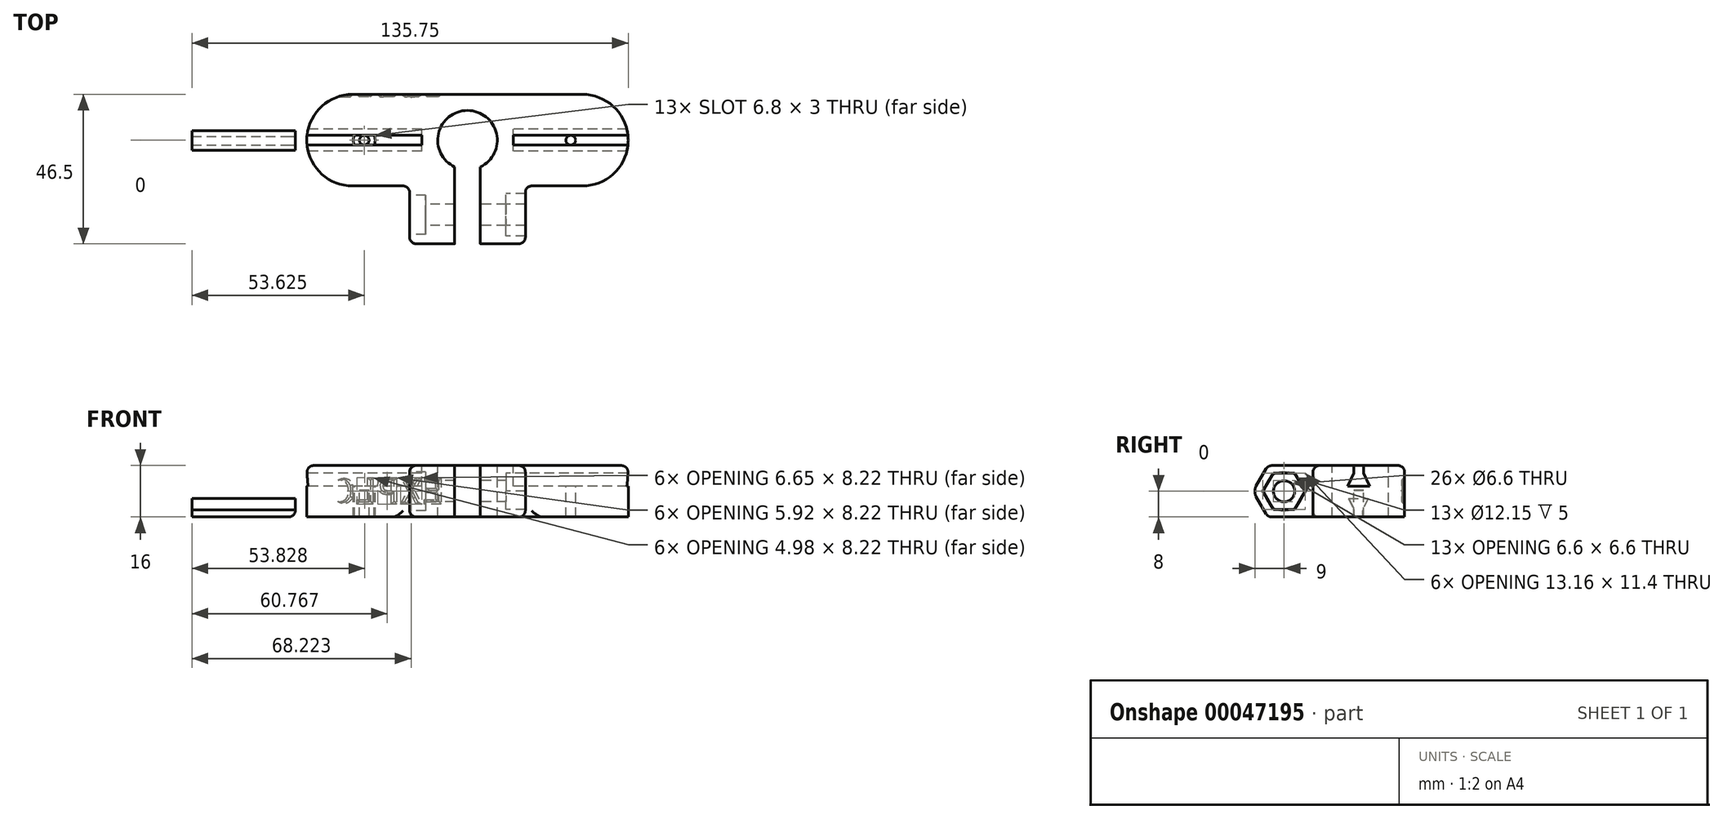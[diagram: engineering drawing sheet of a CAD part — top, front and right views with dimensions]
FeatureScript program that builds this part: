
annotation { "Feature Type Name" : "Feature", "Feature Type Description" : "" }
export const myFeature = defineFeature(function(context is Context, id is Id, definition is map)
    precondition{}
    {
        {
            assignVariable(context, id + "F0", {"name" : "PrintingOffset", "anyValue" : .4});
        }
        {
            assignVariable(context, id + "F1", {"name" : "BoltExtensionWidth", "anyValue" : 14});
        }
        {
            assignVariable(context, id + "F2", {"name" : "DeviceWidth", "anyValue" : 100});
        }
        {
            assignVariable(context, id + "F3", {"name" : "FlexureOpening", "anyValue" : 8});
        }
        {
            assignVariable(context, id + "F4", {"name" : "RodPadding", "anyValue" : 5});
        }
        {
            assignVariable(context, id + "F5", {"name" : "RodDiameter", "anyValue" : 18.5});
        }
        {
            var Q0;
            Q0=qCreatedBy(makeId("Top.planeOp"),FACE);
            var sketch = newSketch(context, id + "F6", { "sketchPlane" : qUnion([Q0])});
            skLineSegment(sketch, "E0", {"start": v(-50, 14.25) * mm, "end": v(-50, -14.25) * mm});
            skLineSegment(sketch, "E1", {"start": v(-50, -14.25) * mm, "end": v(-18, -14.25) * mm});
            skLineSegment(sketch, "E2", {"start": v(-18, -14.25) * mm, "end": v(-18, -32.25) * mm});
            skLineSegment(sketch, "E3", {"start": v(-18, -32.25) * mm, "end": v(-4, -32.25) * mm});
            skLineSegment(sketch, "E4", {"start": v(-4, -32.25) * mm, "end": v(-4, -8.34) * mm});
            skLineSegment(sketch, "E5", {"start": v(-50, 14.25) * mm, "end": v(0, 14.25) * mm});
            skLineSegment(sketch, "E6", {"start": v(0, 35.83) * mm, "end": v(0, -44.2) * mm, "construction": true});
            skLineSegment(sketch, "E7.MirrorCS", {"start": v(50, 14.25) * mm, "end": v(50, -14.25) * mm});
            skLineSegment(sketch, "E8.MirrorCS", {"start": v(50, -14.25) * mm, "end": v(18, -14.25) * mm});
            skLineSegment(sketch, "E9.MirrorCS", {"start": v(18, -14.25) * mm, "end": v(18, -32.25) * mm});
            skLineSegment(sketch, "E10.MirrorCS", {"start": v(18, -32.25) * mm, "end": v(4, -32.25) * mm});
            skLineSegment(sketch, "E11.MirrorCS", {"start": v(4, -32.25) * mm, "end": v(4, -8.34) * mm});
            skLineSegment(sketch, "E12.MirrorCS", {"start": v(50, 14.25) * mm, "end": v(0, 14.25) * mm});
            skArc(sketch, "E13", {"start": v(4, -8.34) * mm, "mid": v(0, 9.25) * mm, "end": v(-4, -8.34) * mm});
            skPoint(sketch, "E14.end.orphan", {"position": v(0, -14.88) * mm});
            skSolve(sketch);
        }
        {
            assignVariable(context, id + "F7", {"name" : "DeviceThickness", "anyValue" : 16});
        }
        {
            var Q0;
            Q0=makeQuery(id+"F6.imprint","IMPRINT",FACE,{"disambiguationData":[TD([[makeQuery(id+"F6.imprint","IMPRINT",EDGE,{"derivedFrom":sQuery(id+"F6.wireOp",EDGE,"E0")}),1.0]])]});
            extrude(context, id + "F8", {"entities" : qUnion([Q0]), "depth" : (getVariable(context, 'DeviceThickness')) * mm});
        }
        {
            assignVariable(context, id + "F9", {"name" : "NailHeadThickness", "anyValue" : 1.25});
        }
        {
            assignVariable(context, id + "F10", {"name" : "NailInsertDepth", "anyValue" : getVariable(context, 'DeviceThickness') * (2 / 5)});
        }
        {
            var Q0;
            Q0=makeQuery(id+"F8.opExtrude","SWEPT_FACE",FACE,{"disambiguationData":[OSD([sQuery(id+"F6.wireOp",EDGE,"E7.MirrorCS")])]});
            var sketch = newSketch(context, id + "F11", { "sketchPlane" : qUnion([Q0])});
            skLineSegment(sketch, "E15.1", {"start": v(14.25, 0) * mm, "end": v(-14.25, 0) * mm});
            skLineSegment(sketch, "E15.5", {"start": v(14.25, 16) * mm, "end": v(-14.25, 16) * mm});
            skLineSegment(sketch, "E15.6", {"start": v(14.25, 16) * mm, "end": v(14.25, 0) * mm});
            skLineSegment(sketch, "E15.7", {"start": v(-14.25, 16) * mm, "end": v(-14.25, 0) * mm});
            skLineSegment(sketch, "E16", {"start": v(0, 0) * mm, "end": v(0, 16) * mm, "construction": true});
            skLineSegment(sketch, "E17", {"start": v(0, 6.4) * mm, "end": v(3.4, 6.4) * mm});
            skLineSegment(sketch, "E18", {"start": v(3.4, 6.4) * mm, "end": v(1.5, 2.4) * mm});
            skLineSegment(sketch, "E19", {"start": v(1.5, 2.4) * mm, "end": v(1.5, 0) * mm});
            skLineSegment(sketch, "E20.MirrorCS", {"start": v(0, 6.4) * mm, "end": v(-3.4, 6.4) * mm});
            skLineSegment(sketch, "E21.MirrorCS", {"start": v(-1.5, 2.4) * mm, "end": v(-1.5, 0) * mm});
            skLineSegment(sketch, "E22.MirrorCS", {"start": v(-3.4, 6.4) * mm, "end": v(-1.5, 2.4) * mm});
            skLineSegment(sketch, "E23", {"start": v(-14.25, 8) * mm, "end": v(14.25, 8) * mm, "construction": true});
            skSolve(sketch);
        }
        {
            assignVariable(context, id + "F12", {"name" : "BoltShaftDiameter", "anyValue" : 6.2 + getVariable(context, 'PrintingOffset')});
        }
        {
            assignVariable(context, id + "F13", {"name" : "BoltHeadDiameter", "anyValue" : 11.75 + getVariable(context, 'PrintingOffset')});
        }
        {
            assignVariable(context, id + "F14", {"name" : "BoltHeadDepth", "anyValue" : 4.6 + getVariable(context, 'PrintingOffset')});
        }
        {
            assignVariable(context, id + "F15", {"name" : "HexNutDepth", "anyValue" : 5.6 + getVariable(context, 'PrintingOffset')});
        }
        {
            var Q0;
            Q0=makeQuery(id+"F8.opExtrude","SWEPT_FACE",FACE,{"disambiguationData":[OSD([sQuery(id+"F6.wireOp",EDGE,"E9.MirrorCS")])]});
            var sketch = newSketch(context, id + "F16", { "sketchPlane" : qUnion([Q0])});
            skLineSegment(sketch, "E24.0", {"start": v(-32.25, 16) * mm, "end": v(-32.25, 0) * mm, "construction": true});
            skLineSegment(sketch, "E24.1", {"start": v(-14.25, 0) * mm, "end": v(-32.25, 0) * mm, "construction": true});
            skLineSegment(sketch, "E24.2", {"start": v(-14.25, 16) * mm, "end": v(-14.25, 0) * mm, "construction": true});
            skLineSegment(sketch, "E24.3", {"start": v(-14.25, 16) * mm, "end": v(-32.25, 16) * mm, "construction": true});
            skLineSegment(sketch, "E25", {"start": v(-32.25, 8) * mm, "end": v(-14.25, 8) * mm, "construction": true});
            skLineSegment(sketch, "E26", {"start": v(-23.25, 16) * mm, "end": v(-23.25, 0) * mm, "construction": true});
            skPoint(sketch, "E27", {"position": v(-23.25, 8) * mm});
            skCircle(sketch, "E28.cCircle", {"center": v(-23.25, 8) * mm, "radius": 5.7 * mm, "construction": true});
            skLineSegment(sketch, "E28.0", {"start": v(-19.96, 13.7) * mm, "end": v(-16.67, 8) * mm});
            skLineSegment(sketch, "E28.1", {"start": v(-16.67, 8) * mm, "end": v(-19.96, 2.3) * mm});
            skLineSegment(sketch, "E28.2", {"start": v(-19.96, 2.3) * mm, "end": v(-26.54, 2.3) * mm});
            skLineSegment(sketch, "E28.3", {"start": v(-26.54, 2.3) * mm, "end": v(-29.83, 8) * mm});
            skLineSegment(sketch, "E28.4", {"start": v(-29.83, 8) * mm, "end": v(-26.54, 13.7) * mm});
            skLineSegment(sketch, "E28.5", {"start": v(-26.54, 13.7) * mm, "end": v(-19.96, 13.7) * mm});
            skPoint(sketch, "E28.0.midPoint", {"position": v(-18.31, 10.85) * mm});
            skSolve(sketch);
        }
        {
            var Q0;
            Q0=makeQuery(id+"F16.imprint","IMPRINT",FACE,{"disambiguationData":[TD([[makeQuery(id+"F16.imprint","IMPRINT",EDGE,{"derivedFrom":sQuery(id+"F16.wireOp",EDGE,"E28.0")}),-1.0]])]});
            extrude(context, id + "F17", {"entities" : qUnion([Q0]), "operationType" : NewBodyOperationType.REMOVE, "oppositeDirection" : true, "depth" : ((getVariable(context, 'BoltExtensionWidth') * 2) + getVariable(context, 'FlexureOpening')) * mm, "hasSecondDirection" : true, "secondDirectionOppositeDirection" : true, "secondDirectionDepth" : (((getVariable(context, 'BoltExtensionWidth') * 2) + getVariable(context, 'FlexureOpening')) - getVariable(context, 'HexNutDepth')) * mm});
        }
        {
            var Q0;
            Q0=sQuery(id+"F16.wireOp",VERTEX,"E27");
            var Q1;
            Q1=makeQuery(id+"F8.opExtrude","SWEPT_BODY",BODY,{"disambiguationData":[OSD([sQuery(id+"F6.wireOp",EDGE,"E0"),sQuery(id+"F6.wireOp",EDGE,"E1"),sQuery(id+"F6.wireOp",EDGE,"E2"),sQuery(id+"F6.wireOp",EDGE,"E3"),sQuery(id+"F6.wireOp",EDGE,"E4"),sQuery(id+"F6.wireOp",EDGE,"E5"),sQuery(id+"F6.wireOp",EDGE,"E7.MirrorCS"),sQuery(id+"F6.wireOp",EDGE,"E8.MirrorCS"),sQuery(id+"F6.wireOp",EDGE,"E9.MirrorCS"),sQuery(id+"F6.wireOp",EDGE,"E10.MirrorCS"),sQuery(id+"F6.wireOp",EDGE,"E11.MirrorCS"),sQuery(id+"F6.wireOp",EDGE,"E12.MirrorCS"),sQuery(id+"F6.wireOp",EDGE,"E13")])]});
            hole(context, id + "F18", {"style" : HoleStyle.C_BORE, "holeDiameter" : (getVariable(context, 'BoltShaftDiameter')) * mm, "cBoreDiameter" : (getVariable(context, 'BoltHeadDiameter')) * mm, "cBoreDepth" : (getVariable(context, 'BoltHeadDepth')) * mm, "endStyle" : HoleEndStyle.THROUGH, "locations" : qUnion([Q0]), "scope" : qUnion([Q1])});
        }
        {
            assignVariable(context, id + "F19", {"name" : "NailInsertWidth", "anyValue" : ((getVariable(context, 'DeviceWidth') - getVariable(context, 'RodDiameter')) - (getVariable(context, 'RodPadding') * 2)) / 2});
        }
        {
            var Q0;
            Q0=makeQuery(id+"F11.imprint","IMPRINT",FACE,{"disambiguationData":[TD([[makeQuery(id+"F11.imprint","IMPRINT",EDGE,{"derivedFrom":sQuery(id+"F11.wireOp",EDGE,"E17")}),-1.0]])]});
            extrude(context, id + "F20", {"entities" : qUnion([Q0]), "operationType" : NewBodyOperationType.REMOVE, "oppositeDirection" : true, "depth" : (getVariable(context, 'NailInsertWidth')) * mm});
        }
        {
            var Q0;
            Q0=makeQuery(id+"F11.imprint","IMPRINT",FACE,{"disambiguationData":[TD([[makeQuery(id+"F11.imprint","IMPRINT",EDGE,{"derivedFrom":sQuery(id+"F11.wireOp",EDGE,"E17")}),-1.0]])]});
            var Q1;
            Q1=makeQuery(id+"F8.opExtrude","SWEPT_FACE",FACE,{"disambiguationData":[OSD([sQuery(id+"F6.wireOp",EDGE,"E0")])]});
            extrude(context, id + "F21", {"entities" : qUnion([Q0]), "operationType" : NewBodyOperationType.REMOVE, "endBound" : BoundingType.UP_TO_SURFACE, "oppositeDirection" : true, "endBoundEntityFace" : qUnion([Q1]), "depth" : 25 * mm, "hasSecondDirection" : true, "secondDirectionOppositeDirection" : true, "secondDirectionDepth" : (getVariable(context, 'DeviceWidth') - getVariable(context, 'NailInsertWidth')) * mm});
        }
        {
            var Q0;
            Q0=makeQuery(id+"F8.opExtrude","CAP_FACE",FACE,{"disambiguationData":[OSD([sQuery(id+"F6.wireOp",EDGE,"E0"),sQuery(id+"F6.wireOp",EDGE,"E1"),sQuery(id+"F6.wireOp",EDGE,"E2"),sQuery(id+"F6.wireOp",EDGE,"E3"),sQuery(id+"F6.wireOp",EDGE,"E4"),sQuery(id+"F6.wireOp",EDGE,"E5"),sQuery(id+"F6.wireOp",EDGE,"E7.MirrorCS"),sQuery(id+"F6.wireOp",EDGE,"E8.MirrorCS"),sQuery(id+"F6.wireOp",EDGE,"E9.MirrorCS"),sQuery(id+"F6.wireOp",EDGE,"E10.MirrorCS"),sQuery(id+"F6.wireOp",EDGE,"E11.MirrorCS"),sQuery(id+"F6.wireOp",EDGE,"E12.MirrorCS"),sQuery(id+"F6.wireOp",EDGE,"E13")])],"isStart":true});
            var sketch = newSketch(context, id + "F22", { "sketchPlane" : qUnion([Q0])});
            skLineSegment(sketch, "E29", {"start": v(0, 39.53) * mm, "end": v(0, -28.34) * mm, "construction": true});
            skCircle(sketch, "E30", {"center": v(-32.12, 0) * mm, "radius": 3.4 * mm});
            skLineSegment(sketch, "E31.0", {"start": v(-50, -1.5) * mm, "end": v(-14.25, -1.5) * mm, "construction": true});
            skLineSegment(sketch, "E31.1", {"start": v(-14.25, -1.5) * mm, "end": v(-14.25, 1.5) * mm, "construction": true});
            skLineSegment(sketch, "E31.2", {"start": v(-50, 1.5) * mm, "end": v(-14.25, 1.5) * mm, "construction": true});
            skCircle(sketch, "E32", {"center": v(-32.12, 0) * mm, "radius": 1.5 * mm});
            skCircle(sketch, "E33.MirrorC", {"center": v(32.13, 0) * mm, "radius": 1.5 * mm});
            skCircle(sketch, "E34.MirrorC", {"center": v(32.13, 0) * mm, "radius": 3.4 * mm});
            skSolve(sketch);
        }
        {
            var Q0;
            {var subQ0=sQuery(id+"F11.wireOp",EDGE,"E15.1");var subQ1=makeQuery(id+"F21.boolean.opBoolean","COPY",EDGE,{"derivedFrom":makeQuery(id+"F21.opExtrude","SWEPT_EDGE",EDGE,{"disambiguationData":[OSD([subQ0,sQuery(id+"F11.wireOp",EDGE,"E21.MirrorCS")])]})});var subQ4=sQuery(id+"F22.wireOp",EDGE,"E30");var subQ5=makeQuery(id+"F22.imprint","INTERSECT",VERTEX,{"disambiguationData":[OD(0.0)],"derivedFrom":[subQ1,subQ4]});Q0=makeQuery(id+"F22.imprint","IMPRINT",FACE,{"disambiguationData":[TD([[makeQuery(id+"F22.imprint","IMPRINT",EDGE,{"disambiguationData":[TD([[subQ5,-1.0]])],"derivedFrom":subQ4}),1.0]])]});}
            var Q1;
            {var subQ0=makeQuery(id+"F21.boolean.opBoolean","COPY",EDGE,{"derivedFrom":makeQuery(id+"F21.opExtrude","SWEPT_EDGE",EDGE,{"disambiguationData":[OSD([sQuery(id+"F11.wireOp",EDGE,"E15.1"),sQuery(id+"F11.wireOp",EDGE,"E19")])]})});var subQ2=sQuery(id+"F22.wireOp",EDGE,"E30");var subQ3=makeQuery(id+"F22.imprint","INTERSECT",VERTEX,{"disambiguationData":[OD(0.0)],"derivedFrom":[subQ0,subQ2]});Q1=makeQuery(id+"F22.imprint","IMPRINT",FACE,{"disambiguationData":[TD([[makeQuery(id+"F22.imprint","IMPRINT",EDGE,{"disambiguationData":[TD([[subQ3,-1.0]])],"derivedFrom":subQ2}),1.0]])]});}
            var Q2;
            {var subQ0=sQuery(id+"F11.wireOp",EDGE,"E15.1");var subQ1=makeQuery(id+"F21.boolean.opBoolean","COPY",EDGE,{"derivedFrom":makeQuery(id+"F21.opExtrude","SWEPT_EDGE",EDGE,{"disambiguationData":[OSD([subQ0,sQuery(id+"F11.wireOp",EDGE,"E21.MirrorCS")])]})});var subQ4=sQuery(id+"F22.wireOp",EDGE,"E30");var subQ5=makeQuery(id+"F22.imprint","INTERSECT",VERTEX,{"disambiguationData":[OD(1.0)],"derivedFrom":[subQ1,subQ4]});Q2=makeQuery(id+"F22.imprint","IMPRINT",FACE,{"disambiguationData":[TD([[makeQuery(id+"F22.imprint","IMPRINT",EDGE,{"disambiguationData":[TD([[subQ5,1.0]])],"derivedFrom":subQ4}),1.0]])]});}
            var Q3;
            {var subQ0=makeQuery(id+"F21.boolean.opBoolean","COPY",EDGE,{"derivedFrom":makeQuery(id+"F21.opExtrude","SWEPT_EDGE",EDGE,{"disambiguationData":[OSD([sQuery(id+"F11.wireOp",EDGE,"E15.1"),sQuery(id+"F11.wireOp",EDGE,"E21.MirrorCS")])]})});var subQ2=sQuery(id+"F22.wireOp",EDGE,"E30");var subQ3=makeQuery(id+"F22.imprint","INTERSECT",VERTEX,{"disambiguationData":[OD(0.0)],"derivedFrom":[subQ0,subQ2]});Q3=makeQuery(id+"F22.imprint","IMPRINT",FACE,{"disambiguationData":[TD([[makeQuery(id+"F22.imprint","IMPRINT",EDGE,{"disambiguationData":[TD([[subQ3,1.0]])],"derivedFrom":subQ2}),1.0]])]});}
            var Q4;
            {var subQ0=makeQuery(id+"F20.boolean.opBoolean","COPY",EDGE,{"derivedFrom":makeQuery(id+"F20.opExtrude","SWEPT_EDGE",EDGE,{"disambiguationData":[OSD([sQuery(id+"F11.wireOp",EDGE,"E15.1"),sQuery(id+"F11.wireOp",EDGE,"E19")])]})});var subQ2=sQuery(id+"F22.wireOp",EDGE,"E34.MirrorC");var subQ4=makeQuery(id+"F22.imprint","INTERSECT",VERTEX,{"disambiguationData":[OD(0.0)],"derivedFrom":[subQ0,subQ2]});Q4=makeQuery(id+"F22.imprint","IMPRINT",FACE,{"disambiguationData":[TD([[makeQuery(id+"F22.imprint","IMPRINT",EDGE,{"disambiguationData":[TD([[subQ4,-1.0]])],"derivedFrom":subQ2}),-1.0]])]});}
            var Q5;
            {var subQ0=sQuery(id+"F11.wireOp",EDGE,"E15.1");var subQ1=makeQuery(id+"F20.boolean.opBoolean","COPY",EDGE,{"derivedFrom":makeQuery(id+"F20.opExtrude","SWEPT_EDGE",EDGE,{"disambiguationData":[OSD([subQ0,sQuery(id+"F11.wireOp",EDGE,"E21.MirrorCS")])]})});var subQ2=sQuery(id+"F22.wireOp",EDGE,"E33.MirrorC");var subQ3=makeQuery(id+"F22.imprint","INTERSECT",VERTEX,{"derivedFrom":[subQ1,subQ2]});Q5=makeQuery(id+"F22.imprint","IMPRINT",FACE,{"disambiguationData":[TD([[makeQuery(id+"F22.imprint","IMPRINT",EDGE,{"disambiguationData":[TD([[subQ3,1.0]])],"derivedFrom":subQ2}),1.0]])]});}
            var Q6;
            {var subQ0=makeQuery(id+"F20.boolean.opBoolean","COPY",EDGE,{"derivedFrom":makeQuery(id+"F20.opExtrude","SWEPT_EDGE",EDGE,{"disambiguationData":[OSD([sQuery(id+"F11.wireOp",EDGE,"E15.1"),sQuery(id+"F11.wireOp",EDGE,"E21.MirrorCS")])]})});var subQ2=sQuery(id+"F22.wireOp",EDGE,"E34.MirrorC");var subQ4=makeQuery(id+"F22.imprint","INTERSECT",VERTEX,{"disambiguationData":[OD(0.0)],"derivedFrom":[subQ0,subQ2]});Q6=makeQuery(id+"F22.imprint","IMPRINT",FACE,{"disambiguationData":[TD([[makeQuery(id+"F22.imprint","IMPRINT",EDGE,{"disambiguationData":[TD([[subQ4,1.0]])],"derivedFrom":subQ2}),-1.0]])]});}
            var Q7;
            {var subQ0=sQuery(id+"F11.wireOp",EDGE,"E15.1");var subQ1=makeQuery(id+"F20.boolean.opBoolean","COPY",EDGE,{"derivedFrom":makeQuery(id+"F20.opExtrude","SWEPT_EDGE",EDGE,{"disambiguationData":[OSD([subQ0,sQuery(id+"F11.wireOp",EDGE,"E21.MirrorCS")])]})});var subQ2=sQuery(id+"F22.wireOp",EDGE,"E33.MirrorC");var subQ3=makeQuery(id+"F22.imprint","INTERSECT",VERTEX,{"derivedFrom":[subQ1,subQ2]});Q7=makeQuery(id+"F22.imprint","IMPRINT",FACE,{"disambiguationData":[TD([[makeQuery(id+"F22.imprint","IMPRINT",EDGE,{"disambiguationData":[TD([[subQ3,-1.0]])],"derivedFrom":subQ2}),1.0]])]});}
            extrude(context, id + "F23", {"entities" : qUnion([Q0, Q1, Q2, Q3, Q4, Q5, Q6, Q7]), "operationType" : NewBodyOperationType.REMOVE, "oppositeDirection" : true, "depth" : (getVariable(context, 'NailInsertDepth') + getVariable(context, 'NailHeadThickness')) * mm});
        }
        {
            var Q0;
            {var subQ0=sQuery(id+"F22.wireOp",EDGE,"E32");var subQ1=sQuery(id+"F11.wireOp",EDGE,"E15.1");var subQ3=makeQuery(id+"F22.imprint","INTERSECT",VERTEX,{"derivedFrom":[makeQuery(id+"F21.boolean.opBoolean","COPY",EDGE,{"derivedFrom":makeQuery(id+"F21.opExtrude","SWEPT_EDGE",EDGE,{"disambiguationData":[OSD([subQ1,sQuery(id+"F11.wireOp",EDGE,"E21.MirrorCS")])]})}),subQ0]});Q0=makeQuery(id+"F22.imprint","IMPRINT",FACE,{"disambiguationData":[TD([[makeQuery(id+"F22.imprint","IMPRINT",EDGE,{"disambiguationData":[TD([[subQ3,-1.0]])],"derivedFrom":subQ0}),1.0]])]});}
            var Q1;
            {var subQ0=sQuery(id+"F22.wireOp",EDGE,"E33.MirrorC");var subQ1=sQuery(id+"F11.wireOp",EDGE,"E15.1");var subQ3=makeQuery(id+"F22.imprint","INTERSECT",VERTEX,{"derivedFrom":[makeQuery(id+"F20.boolean.opBoolean","COPY",EDGE,{"derivedFrom":makeQuery(id+"F20.opExtrude","SWEPT_EDGE",EDGE,{"disambiguationData":[OSD([subQ1,sQuery(id+"F11.wireOp",EDGE,"E21.MirrorCS")])]})}),subQ0]});Q1=makeQuery(id+"F22.imprint","IMPRINT",FACE,{"disambiguationData":[TD([[makeQuery(id+"F22.imprint","IMPRINT",EDGE,{"disambiguationData":[TD([[subQ3,-1.0]])],"derivedFrom":subQ0}),-1.0]])]});}
            extrude(context, id + "F24", {"entities" : qUnion([Q0, Q1]), "operationType" : NewBodyOperationType.REMOVE, "endBound" : BoundingType.THROUGH_ALL, "oppositeDirection" : true, "depth" : 25 * mm});
        }
        {
            var Q0;
            Q0=makeQuery(id+"F11.imprint","IMPRINT",FACE,{"disambiguationData":[TD([[makeQuery(id+"F11.imprint","IMPRINT",EDGE,{"derivedFrom":sQuery(id+"F11.wireOp",EDGE,"E17")}),-1.0]])]});
            extrude(context, id + "F25", {"entities" : qUnion([Q0]), "oppositeDirection" : true, "depth" : (getVariable(context, 'NailInsertWidth')) * mm});
        }
        {
            var Q0;
            Q0=makeQuery(id+"F25.opExtrude","SWEPT_BODY",BODY,{"disambiguationData":[OSD([sQuery(id+"F11.wireOp",EDGE,"E15.1"),sQuery(id+"F11.wireOp",EDGE,"E17"),sQuery(id+"F11.wireOp",EDGE,"E18"),sQuery(id+"F11.wireOp",EDGE,"E19"),sQuery(id+"F11.wireOp",EDGE,"E20.MirrorCS"),sQuery(id+"F11.wireOp",EDGE,"E21.MirrorCS"),sQuery(id+"F11.wireOp",EDGE,"E22.MirrorCS")])]});
            var Q1;
            Q1=makeQuery(id+"F25.opExtrude","CAP_VERTEX",VERTEX,{"disambiguationData":[OSD([sQuery(id+"F11.wireOp",EDGE,"E15.1"),sQuery(id+"F11.wireOp",EDGE,"E21.MirrorCS")])],"isStart":false});
            transform(context, id + "F26", {"entities" : qUnion([Q0]), "transformType" : TransformType.SCALE_UNIFORMLY, "scale" : .9, "makeCopy" : false, "scalePoint" : qUnion([Q1])});
        }
        {
            var Q0;
            Q0=makeQuery(id+"F8.opExtrude","SWEPT_EDGE",EDGE,{"disambiguationData":[OSD([sQuery(id+"F6.wireOp",EDGE,"E0"),sQuery(id+"F6.wireOp",EDGE,"E1")])]});
            var Q1;
            Q1=makeQuery(id+"F8.opExtrude","SWEPT_EDGE",EDGE,{"disambiguationData":[OSD([sQuery(id+"F6.wireOp",EDGE,"E7.MirrorCS"),sQuery(id+"F6.wireOp",EDGE,"E8.MirrorCS")])]});
            var Q2;
            Q2=makeQuery(id+"F8.opExtrude","SWEPT_EDGE",EDGE,{"disambiguationData":[OSD([sQuery(id+"F6.wireOp",EDGE,"E7.MirrorCS"),sQuery(id+"F6.wireOp",EDGE,"E12.MirrorCS")])]});
            var Q3;
            Q3=makeQuery(id+"F8.opExtrude","SWEPT_EDGE",EDGE,{"disambiguationData":[OSD([sQuery(id+"F6.wireOp",EDGE,"E0"),sQuery(id+"F6.wireOp",EDGE,"E5")])]});
            fillet(context, id + "F27", {"entities" : qUnion([Q0, Q1, Q2, Q3]), "radius" : ((getVariable(context, 'RodDiameter') / 2) + getVariable(context, 'RodPadding')) * mm, "tangentPropagation" : true, "allowEdgeOverflow" : false});
        }
        {
            var Q0;
            Q0=makeQuery(id+"F8.opExtrude","SWEPT_BODY",BODY,{"disambiguationData":[OSD([sQuery(id+"F6.wireOp",EDGE,"E0"),sQuery(id+"F6.wireOp",EDGE,"E1"),sQuery(id+"F6.wireOp",EDGE,"E2"),sQuery(id+"F6.wireOp",EDGE,"E3"),sQuery(id+"F6.wireOp",EDGE,"E4"),sQuery(id+"F6.wireOp",EDGE,"E5"),sQuery(id+"F6.wireOp",EDGE,"E7.MirrorCS"),sQuery(id+"F6.wireOp",EDGE,"E8.MirrorCS"),sQuery(id+"F6.wireOp",EDGE,"E9.MirrorCS"),sQuery(id+"F6.wireOp",EDGE,"E10.MirrorCS"),sQuery(id+"F6.wireOp",EDGE,"E11.MirrorCS"),sQuery(id+"F6.wireOp",EDGE,"E12.MirrorCS"),sQuery(id+"F6.wireOp",EDGE,"E13")])]});
            var Q1;
            Q1=sQuery(id+"F11.wireOp",EDGE,"E23");
            transform(context, id + "F28", {"entities" : qUnion([Q0]), "transformType" : TransformType.ROTATION, "transformAxis" : qUnion([Q1]), "angle" : 180 * degree, "makeCopy" : false});
        }
        {
            var Q0;
            Q0=makeQuery(id+"F8.opExtrude","CAP_EDGE",EDGE,{"disambiguationData":[OSD([sQuery(id+"F6.wireOp",EDGE,"E3")])],"isStart":false});
            var Q1;
            Q1=makeQuery(id+"F8.opExtrude","CAP_EDGE",EDGE,{"disambiguationData":[OSD([sQuery(id+"F6.wireOp",EDGE,"E10.MirrorCS")])],"isStart":false});
            var Q2;
            Q2=makeQuery(id+"F8.opExtrude","CAP_EDGE",EDGE,{"disambiguationData":[OSD([sQuery(id+"F6.wireOp",EDGE,"E3")])],"isStart":true});
            var Q3;
            Q3=makeQuery(id+"F8.opExtrude","CAP_EDGE",EDGE,{"disambiguationData":[OSD([sQuery(id+"F6.wireOp",EDGE,"E10.MirrorCS")])],"isStart":true});
            chamfer(context, id + "F29", {"entities" : qUnion([Q0, Q1, Q2, Q3]), "chamferType" : ChamferType.OFFSET_ANGLE, "width" : 4 * mm, "oppositeDirection" : false, "angle" : 60 * degree, "tangentPropagation" : true});
        }
        {
            var Q0;
            {var subQ0=sQuery(id+"F6.wireOp",EDGE,"E0");var subQ1=sQuery(id+"F6.wireOp",EDGE,"E1");Q0=makeQuery(id+"F27.opFillet","BLEND_EDGE",EDGE,{"blendedFrom":[makeQuery(id+"F8.opExtrude","SWEPT_EDGE",EDGE,{"disambiguationData":[OSD([subQ0,subQ1])]}),makeQuery(id+"F8.opExtrude","CAP_FACE",FACE,{"disambiguationData":[OSD([subQ0,subQ1,sQuery(id+"F6.wireOp",EDGE,"E2"),sQuery(id+"F6.wireOp",EDGE,"E3"),sQuery(id+"F6.wireOp",EDGE,"E4"),sQuery(id+"F6.wireOp",EDGE,"E5"),sQuery(id+"F6.wireOp",EDGE,"E7.MirrorCS"),sQuery(id+"F6.wireOp",EDGE,"E8.MirrorCS"),sQuery(id+"F6.wireOp",EDGE,"E9.MirrorCS"),sQuery(id+"F6.wireOp",EDGE,"E10.MirrorCS"),sQuery(id+"F6.wireOp",EDGE,"E11.MirrorCS"),sQuery(id+"F6.wireOp",EDGE,"E12.MirrorCS"),sQuery(id+"F6.wireOp",EDGE,"E13")])],"isStart":false})],"blendedInto":[makeQuery(id+"F8.opExtrude","CAP_FACE",FACE,{"disambiguationData":[OSD([subQ0,subQ1,sQuery(id+"F6.wireOp",EDGE,"E2"),sQuery(id+"F6.wireOp",EDGE,"E3"),sQuery(id+"F6.wireOp",EDGE,"E4"),sQuery(id+"F6.wireOp",EDGE,"E5"),sQuery(id+"F6.wireOp",EDGE,"E7.MirrorCS"),sQuery(id+"F6.wireOp",EDGE,"E8.MirrorCS"),sQuery(id+"F6.wireOp",EDGE,"E9.MirrorCS"),sQuery(id+"F6.wireOp",EDGE,"E10.MirrorCS"),sQuery(id+"F6.wireOp",EDGE,"E11.MirrorCS"),sQuery(id+"F6.wireOp",EDGE,"E12.MirrorCS"),sQuery(id+"F6.wireOp",EDGE,"E13")])],"isStart":false})]});}
            var Q1;
            Q1=makeQuery(id+"F8.opExtrude","CAP_EDGE",EDGE,{"disambiguationData":[OSD([sQuery(id+"F6.wireOp",EDGE,"E2")])],"isStart":false});
            var Q2;
            Q2=makeQuery(id+"F8.opExtrude","CAP_EDGE",EDGE,{"disambiguationData":[OSD([sQuery(id+"F6.wireOp",EDGE,"E10.MirrorCS")])],"isStart":false});
            var Q3;
            Q3=makeQuery(id+"F8.opExtrude","CAP_EDGE",EDGE,{"disambiguationData":[OSD([sQuery(id+"F6.wireOp",EDGE,"E9.MirrorCS")])],"isStart":false});
            var Q4;
            Q4=makeQuery(id+"F8.opExtrude","CAP_EDGE",EDGE,{"disambiguationData":[OSD([sQuery(id+"F6.wireOp",EDGE,"E3")])],"isStart":false});
            var Q5;
            Q5=makeQuery(id+"F8.opExtrude","CAP_EDGE",EDGE,{"disambiguationData":[OSD([sQuery(id+"F6.wireOp",EDGE,"E3")])],"isStart":true});
            var Q6;
            Q6=makeQuery(id+"F8.opExtrude","CAP_EDGE",EDGE,{"disambiguationData":[OSD([sQuery(id+"F6.wireOp",EDGE,"E10.MirrorCS")])],"isStart":true});
            var Q7;
            Q7=makeQuery(id+"F8.opExtrude","CAP_EDGE",EDGE,{"disambiguationData":[OSD([sQuery(id+"F6.wireOp",EDGE,"E9.MirrorCS")])],"isStart":true});
            var Q8;
            Q8=makeQuery(id+"F8.opExtrude","CAP_EDGE",EDGE,{"disambiguationData":[OSD([sQuery(id+"F6.wireOp",EDGE,"E2")])],"isStart":true});
            var Q9;
            Q9=makeQuery(id+"F8.opExtrude","CAP_EDGE",EDGE,{"disambiguationData":[OSD([sQuery(id+"F6.wireOp",EDGE,"E1")])],"isStart":true});
            var Q10;
            {var subQ0=sQuery(id+"F6.wireOp",EDGE,"E0");var subQ1=sQuery(id+"F6.wireOp",EDGE,"E5");Q10=makeQuery(id+"F27.opFillet","BLEND_EDGE",EDGE,{"blendedFrom":[makeQuery(id+"F8.opExtrude","SWEPT_EDGE",EDGE,{"disambiguationData":[OSD([subQ0,subQ1])]}),makeQuery(id+"F8.opExtrude","CAP_FACE",FACE,{"disambiguationData":[OSD([subQ0,sQuery(id+"F6.wireOp",EDGE,"E1"),sQuery(id+"F6.wireOp",EDGE,"E2"),sQuery(id+"F6.wireOp",EDGE,"E3"),sQuery(id+"F6.wireOp",EDGE,"E4"),subQ1,sQuery(id+"F6.wireOp",EDGE,"E7.MirrorCS"),sQuery(id+"F6.wireOp",EDGE,"E8.MirrorCS"),sQuery(id+"F6.wireOp",EDGE,"E9.MirrorCS"),sQuery(id+"F6.wireOp",EDGE,"E10.MirrorCS"),sQuery(id+"F6.wireOp",EDGE,"E11.MirrorCS"),sQuery(id+"F6.wireOp",EDGE,"E12.MirrorCS"),sQuery(id+"F6.wireOp",EDGE,"E13")])],"isStart":true})],"blendedInto":[makeQuery(id+"F8.opExtrude","CAP_FACE",FACE,{"disambiguationData":[OSD([subQ0,sQuery(id+"F6.wireOp",EDGE,"E1"),sQuery(id+"F6.wireOp",EDGE,"E2"),sQuery(id+"F6.wireOp",EDGE,"E3"),sQuery(id+"F6.wireOp",EDGE,"E4"),subQ1,sQuery(id+"F6.wireOp",EDGE,"E7.MirrorCS"),sQuery(id+"F6.wireOp",EDGE,"E8.MirrorCS"),sQuery(id+"F6.wireOp",EDGE,"E9.MirrorCS"),sQuery(id+"F6.wireOp",EDGE,"E10.MirrorCS"),sQuery(id+"F6.wireOp",EDGE,"E11.MirrorCS"),sQuery(id+"F6.wireOp",EDGE,"E12.MirrorCS"),sQuery(id+"F6.wireOp",EDGE,"E13")])],"isStart":true})]});}
            var Q11;
            {var subQ0=sQuery(id+"F6.wireOp",EDGE,"E7.MirrorCS");var subQ1=sQuery(id+"F6.wireOp",EDGE,"E8.MirrorCS");Q11=makeQuery(id+"F27.opFillet","BLEND_EDGE",EDGE,{"blendedFrom":[makeQuery(id+"F8.opExtrude","SWEPT_EDGE",EDGE,{"disambiguationData":[OSD([subQ0,subQ1])]}),makeQuery(id+"F8.opExtrude","CAP_FACE",FACE,{"disambiguationData":[OSD([sQuery(id+"F6.wireOp",EDGE,"E0"),sQuery(id+"F6.wireOp",EDGE,"E1"),sQuery(id+"F6.wireOp",EDGE,"E2"),sQuery(id+"F6.wireOp",EDGE,"E3"),sQuery(id+"F6.wireOp",EDGE,"E4"),sQuery(id+"F6.wireOp",EDGE,"E5"),subQ0,subQ1,sQuery(id+"F6.wireOp",EDGE,"E9.MirrorCS"),sQuery(id+"F6.wireOp",EDGE,"E10.MirrorCS"),sQuery(id+"F6.wireOp",EDGE,"E11.MirrorCS"),sQuery(id+"F6.wireOp",EDGE,"E12.MirrorCS"),sQuery(id+"F6.wireOp",EDGE,"E13")])],"isStart":true})],"blendedInto":[makeQuery(id+"F8.opExtrude","CAP_FACE",FACE,{"disambiguationData":[OSD([sQuery(id+"F6.wireOp",EDGE,"E0"),sQuery(id+"F6.wireOp",EDGE,"E1"),sQuery(id+"F6.wireOp",EDGE,"E2"),sQuery(id+"F6.wireOp",EDGE,"E3"),sQuery(id+"F6.wireOp",EDGE,"E4"),sQuery(id+"F6.wireOp",EDGE,"E5"),subQ0,subQ1,sQuery(id+"F6.wireOp",EDGE,"E9.MirrorCS"),sQuery(id+"F6.wireOp",EDGE,"E10.MirrorCS"),sQuery(id+"F6.wireOp",EDGE,"E11.MirrorCS"),sQuery(id+"F6.wireOp",EDGE,"E12.MirrorCS"),sQuery(id+"F6.wireOp",EDGE,"E13")])],"isStart":true})]});}
            var Q12;
            Q12=makeQuery(id+"F25.opExtrude","CAP_EDGE",EDGE,{"disambiguationData":[OSD([sQuery(id+"F11.wireOp",EDGE,"E15.1")])],"isStart":true});
            var Q13;
            Q13=makeQuery(id+"F8.opExtrude","SWEPT_EDGE",EDGE,{"disambiguationData":[OSD([sQuery(id+"F6.wireOp",EDGE,"E8.MirrorCS"),sQuery(id+"F6.wireOp",EDGE,"E9.MirrorCS")])]});
            var Q14;
            Q14=makeQuery(id+"F8.opExtrude","SWEPT_EDGE",EDGE,{"disambiguationData":[OSD([sQuery(id+"F6.wireOp",EDGE,"E1"),sQuery(id+"F6.wireOp",EDGE,"E2")])]});
            var Q15;
            {var subQ0=sQuery(id+"F6.wireOp",EDGE,"E3");Q15=makeQuery(id+"F29.opChamfer","BLEND_EDGE",EDGE,{"blendedFrom":[makeQuery(id+"F8.opExtrude","CAP_EDGE",EDGE,{"disambiguationData":[OSD([subQ0])],"isStart":true}),makeQuery(id+"F8.opExtrude","CAP_FACE",FACE,{"disambiguationData":[OSD([sQuery(id+"F6.wireOp",EDGE,"E0"),sQuery(id+"F6.wireOp",EDGE,"E1"),sQuery(id+"F6.wireOp",EDGE,"E2"),subQ0,sQuery(id+"F6.wireOp",EDGE,"E4"),sQuery(id+"F6.wireOp",EDGE,"E5"),sQuery(id+"F6.wireOp",EDGE,"E7.MirrorCS"),sQuery(id+"F6.wireOp",EDGE,"E8.MirrorCS"),sQuery(id+"F6.wireOp",EDGE,"E9.MirrorCS"),sQuery(id+"F6.wireOp",EDGE,"E10.MirrorCS"),sQuery(id+"F6.wireOp",EDGE,"E11.MirrorCS"),sQuery(id+"F6.wireOp",EDGE,"E12.MirrorCS"),sQuery(id+"F6.wireOp",EDGE,"E13")])],"isStart":true})],"blendedInto":[makeQuery(id+"F8.opExtrude","CAP_FACE",FACE,{"disambiguationData":[OSD([sQuery(id+"F6.wireOp",EDGE,"E0"),sQuery(id+"F6.wireOp",EDGE,"E1"),sQuery(id+"F6.wireOp",EDGE,"E2"),subQ0,sQuery(id+"F6.wireOp",EDGE,"E4"),sQuery(id+"F6.wireOp",EDGE,"E5"),sQuery(id+"F6.wireOp",EDGE,"E7.MirrorCS"),sQuery(id+"F6.wireOp",EDGE,"E8.MirrorCS"),sQuery(id+"F6.wireOp",EDGE,"E9.MirrorCS"),sQuery(id+"F6.wireOp",EDGE,"E10.MirrorCS"),sQuery(id+"F6.wireOp",EDGE,"E11.MirrorCS"),sQuery(id+"F6.wireOp",EDGE,"E12.MirrorCS"),sQuery(id+"F6.wireOp",EDGE,"E13")])],"isStart":true})]});}
            var Q16;
            {var subQ0=sQuery(id+"F6.wireOp",EDGE,"E3");Q16=makeQuery(id+"F29.opChamfer","BLEND_EDGE",EDGE,{"blendedFrom":[makeQuery(id+"F8.opExtrude","CAP_EDGE",EDGE,{"disambiguationData":[OSD([subQ0])],"isStart":true}),makeQuery(id+"F8.opExtrude","SWEPT_FACE",FACE,{"disambiguationData":[OSD([subQ0])]})],"blendedInto":[makeQuery(id+"F8.opExtrude","SWEPT_FACE",FACE,{"disambiguationData":[OSD([subQ0])]})]});}
            var Q17;
            {var subQ0=sQuery(id+"F6.wireOp",EDGE,"E3");Q17=makeQuery(id+"F29.opChamfer","BLEND_EDGE",EDGE,{"blendedFrom":[makeQuery(id+"F8.opExtrude","CAP_EDGE",EDGE,{"disambiguationData":[OSD([subQ0])],"isStart":false}),makeQuery(id+"F8.opExtrude","SWEPT_FACE",FACE,{"disambiguationData":[OSD([subQ0])]})],"blendedInto":[makeQuery(id+"F8.opExtrude","SWEPT_FACE",FACE,{"disambiguationData":[OSD([subQ0])]})]});}
            var Q18;
            {var subQ0=sQuery(id+"F6.wireOp",EDGE,"E3");Q18=makeQuery(id+"F29.opChamfer","BLEND_EDGE",EDGE,{"blendedFrom":[makeQuery(id+"F8.opExtrude","CAP_EDGE",EDGE,{"disambiguationData":[OSD([subQ0])],"isStart":false}),makeQuery(id+"F8.opExtrude","CAP_FACE",FACE,{"disambiguationData":[OSD([sQuery(id+"F6.wireOp",EDGE,"E0"),sQuery(id+"F6.wireOp",EDGE,"E1"),sQuery(id+"F6.wireOp",EDGE,"E2"),subQ0,sQuery(id+"F6.wireOp",EDGE,"E4"),sQuery(id+"F6.wireOp",EDGE,"E5"),sQuery(id+"F6.wireOp",EDGE,"E7.MirrorCS"),sQuery(id+"F6.wireOp",EDGE,"E8.MirrorCS"),sQuery(id+"F6.wireOp",EDGE,"E9.MirrorCS"),sQuery(id+"F6.wireOp",EDGE,"E10.MirrorCS"),sQuery(id+"F6.wireOp",EDGE,"E11.MirrorCS"),sQuery(id+"F6.wireOp",EDGE,"E12.MirrorCS"),sQuery(id+"F6.wireOp",EDGE,"E13")])],"isStart":false})],"blendedInto":[makeQuery(id+"F8.opExtrude","CAP_FACE",FACE,{"disambiguationData":[OSD([sQuery(id+"F6.wireOp",EDGE,"E0"),sQuery(id+"F6.wireOp",EDGE,"E1"),sQuery(id+"F6.wireOp",EDGE,"E2"),subQ0,sQuery(id+"F6.wireOp",EDGE,"E4"),sQuery(id+"F6.wireOp",EDGE,"E5"),sQuery(id+"F6.wireOp",EDGE,"E7.MirrorCS"),sQuery(id+"F6.wireOp",EDGE,"E8.MirrorCS"),sQuery(id+"F6.wireOp",EDGE,"E9.MirrorCS"),sQuery(id+"F6.wireOp",EDGE,"E10.MirrorCS"),sQuery(id+"F6.wireOp",EDGE,"E11.MirrorCS"),sQuery(id+"F6.wireOp",EDGE,"E12.MirrorCS"),sQuery(id+"F6.wireOp",EDGE,"E13")])],"isStart":false})]});}
            var Q19;
            {var subQ0=sQuery(id+"F6.wireOp",EDGE,"E10.MirrorCS");Q19=makeQuery(id+"F29.opChamfer","BLEND_EDGE",EDGE,{"blendedFrom":[makeQuery(id+"F8.opExtrude","CAP_EDGE",EDGE,{"disambiguationData":[OSD([subQ0])],"isStart":false}),makeQuery(id+"F8.opExtrude","CAP_FACE",FACE,{"disambiguationData":[OSD([sQuery(id+"F6.wireOp",EDGE,"E0"),sQuery(id+"F6.wireOp",EDGE,"E1"),sQuery(id+"F6.wireOp",EDGE,"E2"),sQuery(id+"F6.wireOp",EDGE,"E3"),sQuery(id+"F6.wireOp",EDGE,"E4"),sQuery(id+"F6.wireOp",EDGE,"E5"),sQuery(id+"F6.wireOp",EDGE,"E7.MirrorCS"),sQuery(id+"F6.wireOp",EDGE,"E8.MirrorCS"),sQuery(id+"F6.wireOp",EDGE,"E9.MirrorCS"),subQ0,sQuery(id+"F6.wireOp",EDGE,"E11.MirrorCS"),sQuery(id+"F6.wireOp",EDGE,"E12.MirrorCS"),sQuery(id+"F6.wireOp",EDGE,"E13")])],"isStart":false})],"blendedInto":[makeQuery(id+"F8.opExtrude","CAP_FACE",FACE,{"disambiguationData":[OSD([sQuery(id+"F6.wireOp",EDGE,"E0"),sQuery(id+"F6.wireOp",EDGE,"E1"),sQuery(id+"F6.wireOp",EDGE,"E2"),sQuery(id+"F6.wireOp",EDGE,"E3"),sQuery(id+"F6.wireOp",EDGE,"E4"),sQuery(id+"F6.wireOp",EDGE,"E5"),sQuery(id+"F6.wireOp",EDGE,"E7.MirrorCS"),sQuery(id+"F6.wireOp",EDGE,"E8.MirrorCS"),sQuery(id+"F6.wireOp",EDGE,"E9.MirrorCS"),subQ0,sQuery(id+"F6.wireOp",EDGE,"E11.MirrorCS"),sQuery(id+"F6.wireOp",EDGE,"E12.MirrorCS"),sQuery(id+"F6.wireOp",EDGE,"E13")])],"isStart":false})]});}
            var Q20;
            {var subQ0=sQuery(id+"F6.wireOp",EDGE,"E10.MirrorCS");Q20=makeQuery(id+"F29.opChamfer","BLEND_EDGE",EDGE,{"blendedFrom":[makeQuery(id+"F8.opExtrude","CAP_EDGE",EDGE,{"disambiguationData":[OSD([subQ0])],"isStart":false}),makeQuery(id+"F8.opExtrude","SWEPT_FACE",FACE,{"disambiguationData":[OSD([subQ0])]})],"blendedInto":[makeQuery(id+"F8.opExtrude","SWEPT_FACE",FACE,{"disambiguationData":[OSD([subQ0])]})]});}
            var Q21;
            {var subQ0=sQuery(id+"F6.wireOp",EDGE,"E10.MirrorCS");Q21=makeQuery(id+"F29.opChamfer","BLEND_EDGE",EDGE,{"blendedFrom":[makeQuery(id+"F8.opExtrude","CAP_EDGE",EDGE,{"disambiguationData":[OSD([subQ0])],"isStart":true}),makeQuery(id+"F8.opExtrude","SWEPT_FACE",FACE,{"disambiguationData":[OSD([subQ0])]})],"blendedInto":[makeQuery(id+"F8.opExtrude","SWEPT_FACE",FACE,{"disambiguationData":[OSD([subQ0])]})]});}
            var Q22;
            {var subQ0=sQuery(id+"F6.wireOp",EDGE,"E10.MirrorCS");Q22=makeQuery(id+"F29.opChamfer","BLEND_EDGE",EDGE,{"blendedFrom":[makeQuery(id+"F8.opExtrude","CAP_EDGE",EDGE,{"disambiguationData":[OSD([subQ0])],"isStart":true}),makeQuery(id+"F8.opExtrude","CAP_FACE",FACE,{"disambiguationData":[OSD([sQuery(id+"F6.wireOp",EDGE,"E0"),sQuery(id+"F6.wireOp",EDGE,"E1"),sQuery(id+"F6.wireOp",EDGE,"E2"),sQuery(id+"F6.wireOp",EDGE,"E3"),sQuery(id+"F6.wireOp",EDGE,"E4"),sQuery(id+"F6.wireOp",EDGE,"E5"),sQuery(id+"F6.wireOp",EDGE,"E7.MirrorCS"),sQuery(id+"F6.wireOp",EDGE,"E8.MirrorCS"),sQuery(id+"F6.wireOp",EDGE,"E9.MirrorCS"),subQ0,sQuery(id+"F6.wireOp",EDGE,"E11.MirrorCS"),sQuery(id+"F6.wireOp",EDGE,"E12.MirrorCS"),sQuery(id+"F6.wireOp",EDGE,"E13")])],"isStart":true})],"blendedInto":[makeQuery(id+"F8.opExtrude","CAP_FACE",FACE,{"disambiguationData":[OSD([sQuery(id+"F6.wireOp",EDGE,"E0"),sQuery(id+"F6.wireOp",EDGE,"E1"),sQuery(id+"F6.wireOp",EDGE,"E2"),sQuery(id+"F6.wireOp",EDGE,"E3"),sQuery(id+"F6.wireOp",EDGE,"E4"),sQuery(id+"F6.wireOp",EDGE,"E5"),sQuery(id+"F6.wireOp",EDGE,"E7.MirrorCS"),sQuery(id+"F6.wireOp",EDGE,"E8.MirrorCS"),sQuery(id+"F6.wireOp",EDGE,"E9.MirrorCS"),subQ0,sQuery(id+"F6.wireOp",EDGE,"E11.MirrorCS"),sQuery(id+"F6.wireOp",EDGE,"E12.MirrorCS"),sQuery(id+"F6.wireOp",EDGE,"E13")])],"isStart":true})]});}
            var Q23;
            Q23=makeQuery(id+"F29.opChamfer","BLEND_EDGE",EDGE,{"blendedFrom":[makeQuery(id+"F8.opExtrude","CAP_EDGE",EDGE,{"disambiguationData":[OSD([sQuery(id+"F6.wireOp",EDGE,"E3")])],"isStart":true}),makeQuery(id+"F8.opExtrude","SWEPT_FACE",FACE,{"disambiguationData":[OSD([sQuery(id+"F6.wireOp",EDGE,"E2")])]})],"blendedInto":[makeQuery(id+"F8.opExtrude","SWEPT_FACE",FACE,{"disambiguationData":[OSD([sQuery(id+"F6.wireOp",EDGE,"E2")])]})]});
            var Q24;
            Q24=makeQuery(id+"F8.opExtrude","SWEPT_EDGE",EDGE,{"disambiguationData":[OSD([sQuery(id+"F6.wireOp",EDGE,"E2"),sQuery(id+"F6.wireOp",EDGE,"E3")])]});
            var Q25;
            Q25=makeQuery(id+"F29.opChamfer","BLEND_EDGE",EDGE,{"blendedFrom":[makeQuery(id+"F8.opExtrude","CAP_EDGE",EDGE,{"disambiguationData":[OSD([sQuery(id+"F6.wireOp",EDGE,"E3")])],"isStart":false}),makeQuery(id+"F8.opExtrude","SWEPT_FACE",FACE,{"disambiguationData":[OSD([sQuery(id+"F6.wireOp",EDGE,"E2")])]})],"blendedInto":[makeQuery(id+"F8.opExtrude","SWEPT_FACE",FACE,{"disambiguationData":[OSD([sQuery(id+"F6.wireOp",EDGE,"E2")])]})]});
            var Q26;
            Q26=makeQuery(id+"F29.opChamfer","BLEND_EDGE",EDGE,{"blendedFrom":[makeQuery(id+"F8.opExtrude","CAP_EDGE",EDGE,{"disambiguationData":[OSD([sQuery(id+"F6.wireOp",EDGE,"E10.MirrorCS")])],"isStart":true}),makeQuery(id+"F8.opExtrude","SWEPT_FACE",FACE,{"disambiguationData":[OSD([sQuery(id+"F6.wireOp",EDGE,"E9.MirrorCS")])]})],"blendedInto":[makeQuery(id+"F8.opExtrude","SWEPT_FACE",FACE,{"disambiguationData":[OSD([sQuery(id+"F6.wireOp",EDGE,"E9.MirrorCS")])]})]});
            var Q27;
            Q27=makeQuery(id+"F8.opExtrude","SWEPT_EDGE",EDGE,{"disambiguationData":[OSD([sQuery(id+"F6.wireOp",EDGE,"E9.MirrorCS"),sQuery(id+"F6.wireOp",EDGE,"E10.MirrorCS")])]});
            var Q28;
            Q28=makeQuery(id+"F29.opChamfer","BLEND_EDGE",EDGE,{"blendedFrom":[makeQuery(id+"F8.opExtrude","CAP_EDGE",EDGE,{"disambiguationData":[OSD([sQuery(id+"F6.wireOp",EDGE,"E10.MirrorCS")])],"isStart":false}),makeQuery(id+"F8.opExtrude","SWEPT_FACE",FACE,{"disambiguationData":[OSD([sQuery(id+"F6.wireOp",EDGE,"E9.MirrorCS")])]})],"blendedInto":[makeQuery(id+"F8.opExtrude","SWEPT_FACE",FACE,{"disambiguationData":[OSD([sQuery(id+"F6.wireOp",EDGE,"E9.MirrorCS")])]})]});
            fillet(context, id + "F30", {"entities" : qUnion([Q0, Q1, Q2, Q3, Q4, Q5, Q6, Q7, Q8, Q9, Q10, Q11, Q12, Q13, Q14, Q15, Q16, Q17, Q18, Q19, Q20, Q21, Q22, Q23, Q24, Q25, Q26, Q27, Q28]), "radius" : 2 * mm, "tangentPropagation" : true, "allowEdgeOverflow" : false});
        }
        {
            var Q0;
            Q0=makeQuery(id+"F8.opExtrude","SWEPT_FACE",FACE,{"disambiguationData":[OSD([sQuery(id+"F6.wireOp",EDGE,"E5"),sQuery(id+"F6.wireOp",EDGE,"E12.MirrorCS")])]});
            var sketch = newSketch(context, id + "F31", { "sketchPlane" : qUnion([Q0])});
            skText(sketch, "E35", { "text": "EXPLO", "fontName": "NotoSansCJKsc-Bold.otf"});
            skPoint(sketch, "E36", {"position": v(-117.79, 8) * mm});
            skLineSegment(sketch, "E37.0", {"start": v(-135.75, 2) * mm, "end": v(-64.25, 2) * mm, "construction": true});
            skLineSegment(sketch, "E37.1", {"start": v(-135.75, 14) * mm, "end": v(-135.75, 2) * mm, "construction": true});
            skLineSegment(sketch, "E37.2", {"start": v(-64.25, 14) * mm, "end": v(-135.75, 14) * mm, "construction": true});
            skLineSegment(sketch, "E37.3", {"start": v(-64.25, 2) * mm, "end": v(-64.25, 14) * mm, "construction": true});
            skLineSegment(sketch, "E38", {"start": v(-100, 14) * mm, "end": v(-100, 2) * mm, "construction": true});
            skLineSegment(sketch, "E39", {"start": v(-135.75, 8) * mm, "end": v(-64.25, 8) * mm, "construction": true});
            const initialGuessF31  = {"E35": [-0.09279, 0.004, 1, 0, 0.008]};
            skSetInitialGuess(sketch, initialGuessF31);
            skSolve(sketch);
        }
        {
            var Q0;
            Q0=makeQuery(id+"F31.imprint","IMPRINT",FACE,{"disambiguationData":[TD([[makeQuery(id+"F31.imprint","IMPRINT",EDGE,{"derivedFrom":sQuery(id+"F31.wireOp",EDGE,"E35.sketch_text.stroke-0")}),1.0]])]});
            var Q1;
            Q1=makeQuery(id+"F31.imprint","IMPRINT",FACE,{"disambiguationData":[TD([[makeQuery(id+"F31.imprint","IMPRINT",EDGE,{"derivedFrom":sQuery(id+"F31.wireOp",EDGE,"E35.sketch_text.stroke-12")}),1.0]])]});
            var Q2;
            Q2=makeQuery(id+"F31.imprint","IMPRINT",FACE,{"disambiguationData":[TD([[makeQuery(id+"F31.imprint","IMPRINT",EDGE,{"derivedFrom":sQuery(id+"F31.wireOp",EDGE,"E35.sketch_text.stroke-30")}),1.0]])]});
            var Q3;
            Q3=makeQuery(id+"F31.imprint","IMPRINT",FACE,{"disambiguationData":[TD([[makeQuery(id+"F31.imprint","IMPRINT",EDGE,{"derivedFrom":sQuery(id+"F31.wireOp",EDGE,"E35.sketch_text.stroke-42")}),1.0]])]});
            var Q4;
            Q4=makeQuery(id+"F31.imprint","IMPRINT",FACE,{"disambiguationData":[TD([[makeQuery(id+"F31.imprint","IMPRINT",EDGE,{"derivedFrom":sQuery(id+"F31.wireOp",EDGE,"E35.sketch_text.stroke-48")}),1.0]])]});
            extrude(context, id + "F32", {"entities" : qUnion([Q0, Q1, Q2, Q3, Q4]), "operationType" : NewBodyOperationType.REMOVE, "oppositeDirection" : true, "depth" : 2 * mm, "hasDraft" : true, "draftAngle" : 45 * degree, "draftPullDirection" : true});
        }
    });
